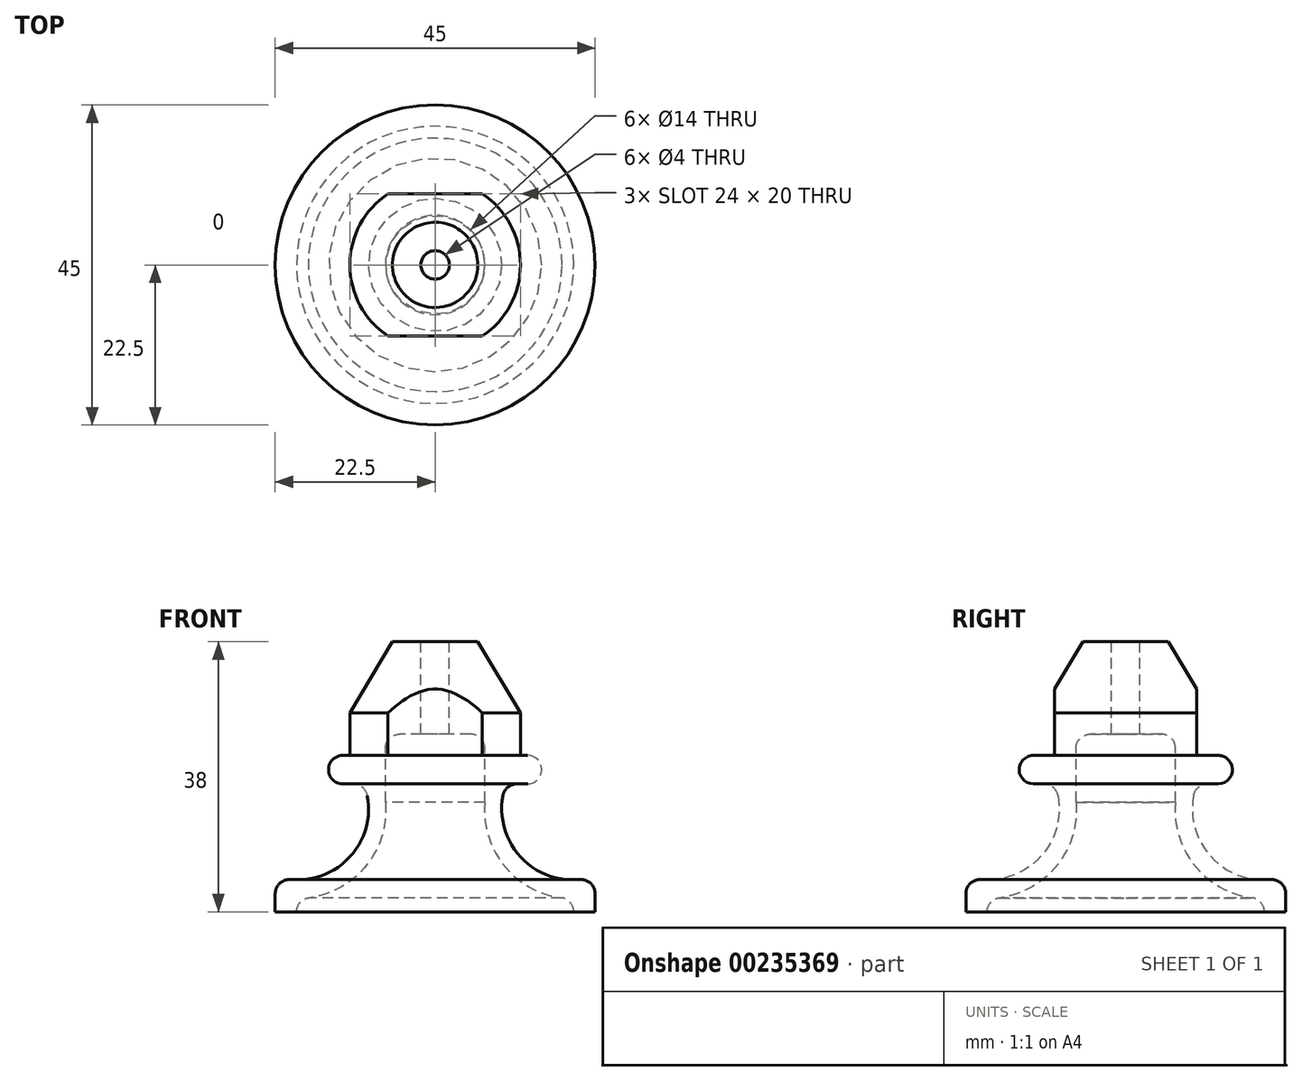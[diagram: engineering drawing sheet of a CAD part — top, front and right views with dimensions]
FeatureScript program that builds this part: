
annotation { "Feature Type Name" : "Feature", "Feature Type Description" : "" }
export const myFeature = defineFeature(function(context is Context, id is Id, definition is map)
    precondition{}
    {
        {
            var Q0;
            Q0=qCreatedBy(makeId("Front.planeOp"),FACE);
            var sketch = newSketch(context, id + "F0", { "sketchPlane" : qUnion([Q0])});
            skPoint(sketch, "E0.visualSharp", {"position": v(1145.61, 20) * mm});
            skLineSegment(sketch, "E1", {"start": v(0, 64.98) * mm, "end": v(0, 0) * mm});
            skLineSegment(sketch, "E2", {"start": v(0, 0) * mm, "end": v(-54.09, 0) * mm});
            skLineSegment(sketch, "E3", {"start": v(0, 38) * mm, "end": v(-6, 38) * mm});
            skLineSegment(sketch, "E4", {"start": v(-6, 38) * mm, "end": v(-12, 28) * mm});
            skLineSegment(sketch, "E5", {"start": v(-12, 28) * mm, "end": v(-12, 22) * mm});
            skLineSegment(sketch, "E6", {"start": v(-12, 22) * mm, "end": v(-15, 22) * mm});
            skLineSegment(sketch, "E7", {"start": v(-15, 22) * mm, "end": v(-15, 18) * mm});
            skLineSegment(sketch, "E8", {"start": v(-22.5, 2.55) * mm, "end": v(-22.5, 0) * mm});
            skLineSegment(sketch, "E9", {"start": v(-2, 25) * mm, "end": v(0, 25) * mm});
            skLineSegment(sketch, "E10", {"start": v(-2, 25) * mm, "end": v(-2, 38) * mm});
            skLineSegment(sketch, "E11", {"start": v(0, 0) * mm, "end": v(-19.5, 0) * mm});
            skLineSegment(sketch, "E12", {"start": v(-2, 25) * mm, "end": v(-5, 25) * mm});
            skLineSegment(sketch, "E13", {"start": v(-15, 18) * mm, "end": v(-11.5, 18) * mm});
            skArc(sketch, "E14", {"start": v(-20.31, 4.54) * mm, "mid": v(-11.97, 7.77) * mm, "end": v(-9.54, 16.38) * mm});
            skArc(sketch, "E15.trimOffspring", {"start": v(-17.84, 1.97) * mm, "mid": v(-9.7, 6.5) * mm, "end": v(-7, 15.41) * mm});
            skLineSegment(sketch, "E16", {"start": v(-7, 23) * mm, "end": v(-7, 15.41) * mm});
            skPoint(sketch, "E17.visualSharp", {"position": v(-22.5, 5) * mm});
            skArc(sketch, "E17.filletArc", {"start": v(-20.31, 4.54) * mm, "mid": v(-21.85, 4.03) * mm, "end": v(-22.5, 2.55) * mm});
            skPoint(sketch, "E18.visualSharp", {"position": v(-10, 18) * mm});
            skArc(sketch, "E18.filletArc", {"start": v(-9.54, 16.38) * mm, "mid": v(-10.23, 17.54) * mm, "end": v(-11.5, 18) * mm});
            skPoint(sketch, "E19.visualSharp", {"position": v(-7, 25) * mm});
            skArc(sketch, "E19.filletArc", {"start": v(-5, 25) * mm, "mid": v(-6.41, 24.41) * mm, "end": v(-7, 23) * mm});
            skArc(sketch, "E20", {"start": v(-17.84, 1.97) * mm, "mid": v(-19.03, 1.29) * mm, "end": v(-19.5, 0) * mm});
            skSolve(sketch);
        }
        {
            var Q0;
            {var subQ4=sQuery(id+"F0.wireOp",EDGE,"E4");Q0=makeQuery(id+"F0.imprint","IMPRINT",FACE,{"disambiguationData":[TD([[makeQuery(id+"F0.imprint","IMPRINT",EDGE,{"derivedFrom":subQ4}),1.0]])]});}
            var Q1;
            Q1=sQuery(id+"F0.wireOp",EDGE,"E1");
            revolve(context, id + "F1", {"entities" : qUnion([Q0]), "axis" : qUnion([Q1]), "revolveType" : RevolveType.FULL});
        }
        {
            var Q0;
            Q0=makeQuery(id+"F1.opRevolve","SWEPT_EDGE",EDGE,{"disambiguationData":[OSD([sQuery(id+"F0.wireOp",EDGE,"E6"),sQuery(id+"F0.wireOp",EDGE,"E7")])]});
            fillet(context, id + "F2", {"entities" : qUnion([Q0]), "radius" : 2 * mm, "tangentPropagation" : true, "allowEdgeOverflow" : false});
        }
        {
            var Q0;
            Q0=makeQuery(id+"F1.opRevolve","SWEPT_EDGE",EDGE,{"disambiguationData":[OSD([sQuery(id+"F0.wireOp",EDGE,"E7"),sQuery(id+"F0.wireOp",EDGE,"E13")])]});
            fillet(context, id + "F3", {"entities" : qUnion([Q0]), "radius" : 2 * mm, "tangentPropagation" : true, "allowEdgeOverflow" : false});
        }
        {
            var Q0;
            Q0=makeQuery(id+"F1.opRevolve","SWEPT_FACE",FACE,{"disambiguationData":[OSD([sQuery(id+"F0.wireOp",EDGE,"E3")])]});
            var sketch = newSketch(context, id + "F4", { "sketchPlane" : qUnion([Q0])});
            skCircle(sketch, "E21.0", {"center": v(0, 0) * mm, "radius": 12 * mm});
            skLineSegment(sketch, "E22.bottom", {"start": v(6.63, -10) * mm, "end": v(-6.63, -10) * mm});
            skLineSegment(sketch, "E22.top", {"start": v(6.63, 10) * mm, "end": v(-6.63, 10) * mm});
            skLineSegment(sketch, "E22.left", {"start": v(6.63, -10) * mm, "end": v(6.63, 10) * mm});
            skLineSegment(sketch, "E22.right", {"start": v(-6.63, -10) * mm, "end": v(-6.63, 10) * mm});
            skSolve(sketch);
        }
        {
            var Q0;
            {var subQ0=sQuery(id+"F4.wireOp",EDGE,"E22.top");Q0=makeQuery(id+"F4.imprint","IMPRINT",FACE,{"disambiguationData":[TD([[makeQuery(id+"F4.imprint","IMPRINT",EDGE,{"derivedFrom":subQ0}),-1.0]])]});}
            var Q1;
            {var subQ0=sQuery(id+"F4.wireOp",EDGE,"E22.bottom");Q1=makeQuery(id+"F4.imprint","IMPRINT",FACE,{"disambiguationData":[TD([[makeQuery(id+"F4.imprint","IMPRINT",EDGE,{"derivedFrom":subQ0}),1.0]])]});}
            extrude(context, id + "F5", {"entities" : qUnion([Q0, Q1]), "operationType" : NewBodyOperationType.REMOVE, "oppositeDirection" : true, "depth" : 16 * mm});
        }
    });
